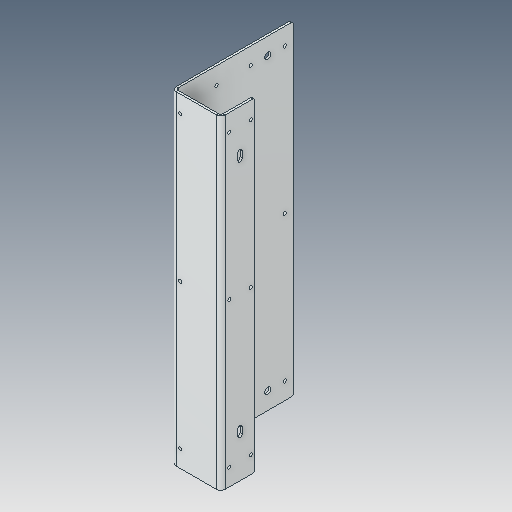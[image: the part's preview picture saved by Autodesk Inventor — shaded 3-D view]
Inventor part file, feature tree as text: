
AUTODESK INVENTOR PART (.ipt)
format: ipt  version: 2023.5 (Build 275446000, 446)  size: 125,952 bytes
history: native  units: in
note: dims shown in document units (in); Inventor stores cm internally (conversion verified against a paired STEP export)
features: fillet x1
ambient origin geometry x8: Origin, YZ Plane, XZ Plane, XY Plane, X Axis, Y Axis, Z Axis, Center Point
bodies: Solid1 (feature_tree)
feature tree (1):
  fillet  "Fillet1"  [1 undecoded]
note: 1 required parameter value undecoded (feature->parameter linkage not recoverable at this tier; creation-order binding heuristic only, values carry confidence <= 0.55)
